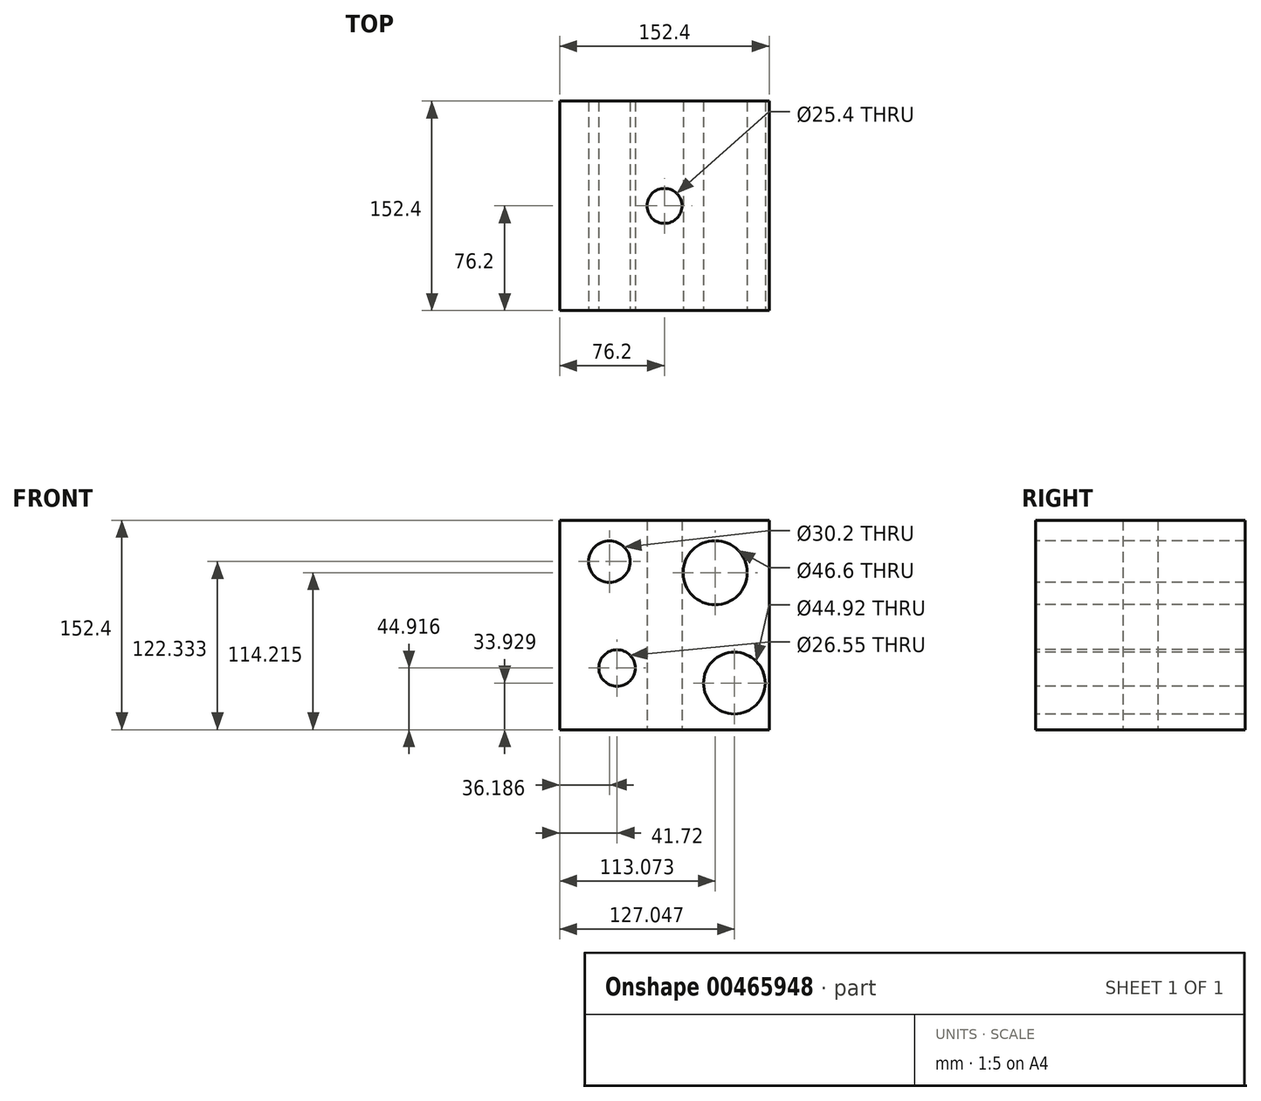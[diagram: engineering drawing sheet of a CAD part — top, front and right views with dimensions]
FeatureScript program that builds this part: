
annotation { "Feature Type Name" : "Feature", "Feature Type Description" : "" }
export const myFeature = defineFeature(function(context is Context, id is Id, definition is map)
    precondition{}
    {
        {
            var Q0;
            Q0=qCreatedBy(makeId("Top.planeOp"),FACE);
            var sketch = newSketch(context, id + "F0", { "sketchPlane" : qUnion([Q0])});
            skLineSegment(sketch, "E0.bottom", {"start": v(76.2, 76.2) * mm, "end": v(-76.2, 76.2) * mm});
            skLineSegment(sketch, "E0.top", {"start": v(76.2, -76.2) * mm, "end": v(-76.2, -76.2) * mm});
            skLineSegment(sketch, "E0.left", {"start": v(76.2, 76.2) * mm, "end": v(76.2, -76.2) * mm});
            skLineSegment(sketch, "E0.right", {"start": v(-76.2, 76.2) * mm, "end": v(-76.2, -76.2) * mm});
            skPoint(sketch, "E0.middle", {"position": v(0, 0) * mm});
            skCircle(sketch, "E1", {"center": v(0, 0) * mm, "radius": 12.7 * mm});
            skSolve(sketch);
        }
        {
            var Q0;
            Q0=makeQuery(id+"F0.imprint","IMPRINT",FACE,{"disambiguationData":[TD([[makeQuery(id+"F0.imprint","IMPRINT",EDGE,{"derivedFrom":sQuery(id+"F0.wireOp",EDGE,"E0.bottom")}),1.0]])]});
            extrude(context, id + "F1", {"entities" : qUnion([Q0]), "depth" : 152.4 * mm});
        }
        {
            var Q0;
            Q0=makeQuery(id+"F1.opExtrude","SWEPT_FACE",FACE,{"disambiguationData":[OSD([sQuery(id+"F0.wireOp",EDGE,"E0.top")])]});
            var sketch = newSketch(context, id + "F2", { "sketchPlane" : qUnion([Q0])});
            skCircle(sketch, "E2", {"center": v(-40.01, 122.33) * mm, "radius": 15.1 * mm});
            skCircle(sketch, "E3", {"center": v(36.87, 114.22) * mm, "radius": 23.3 * mm});
            skCircle(sketch, "E4", {"center": v(50.85, 33.93) * mm, "radius": 22.46 * mm});
            skCircle(sketch, "E5", {"center": v(-34.48, 44.92) * mm, "radius": 13.27 * mm});
            skSolve(sketch);
        }
        {
            var Q0;
            Q0=makeQuery(id+"F2.imprint","IMPRINT",FACE,{"disambiguationData":[TD([[makeQuery(id+"F2.imprint","IMPRINT",EDGE,{"derivedFrom":sQuery(id+"F2.wireOp",EDGE,"E2")}),1.0]])]});
            var Q1;
            Q1=makeQuery(id+"F2.imprint","IMPRINT",FACE,{"disambiguationData":[TD([[makeQuery(id+"F2.imprint","IMPRINT",EDGE,{"derivedFrom":sQuery(id+"F2.wireOp",EDGE,"E3")}),1.0]])]});
            var Q2;
            Q2=makeQuery(id+"F2.imprint","IMPRINT",FACE,{"disambiguationData":[TD([[makeQuery(id+"F2.imprint","IMPRINT",EDGE,{"derivedFrom":sQuery(id+"F2.wireOp",EDGE,"E4")}),1.0]])]});
            var Q3;
            Q3=makeQuery(id+"F2.imprint","IMPRINT",FACE,{"disambiguationData":[TD([[makeQuery(id+"F2.imprint","IMPRINT",EDGE,{"derivedFrom":sQuery(id+"F2.wireOp",EDGE,"E5")}),1.0]])]});
            extrude(context, id + "F3", {"entities" : qUnion([Q0, Q1, Q2, Q3]), "operationType" : NewBodyOperationType.REMOVE, "endBound" : BoundingType.THROUGH_ALL, "oppositeDirection" : true, "depth" : 25.4 * mm});
        }
        {
            var Q0;
            Q0=sQuery(id+"F2.wireOp",EDGE,"E3");
            extrude(context, id + "F4", {"bodyType" : ToolBodyType.SURFACE, "surfaceEntities" : qUnion([Q0]), "depth" : 25.4 * mm});
        }
    });
